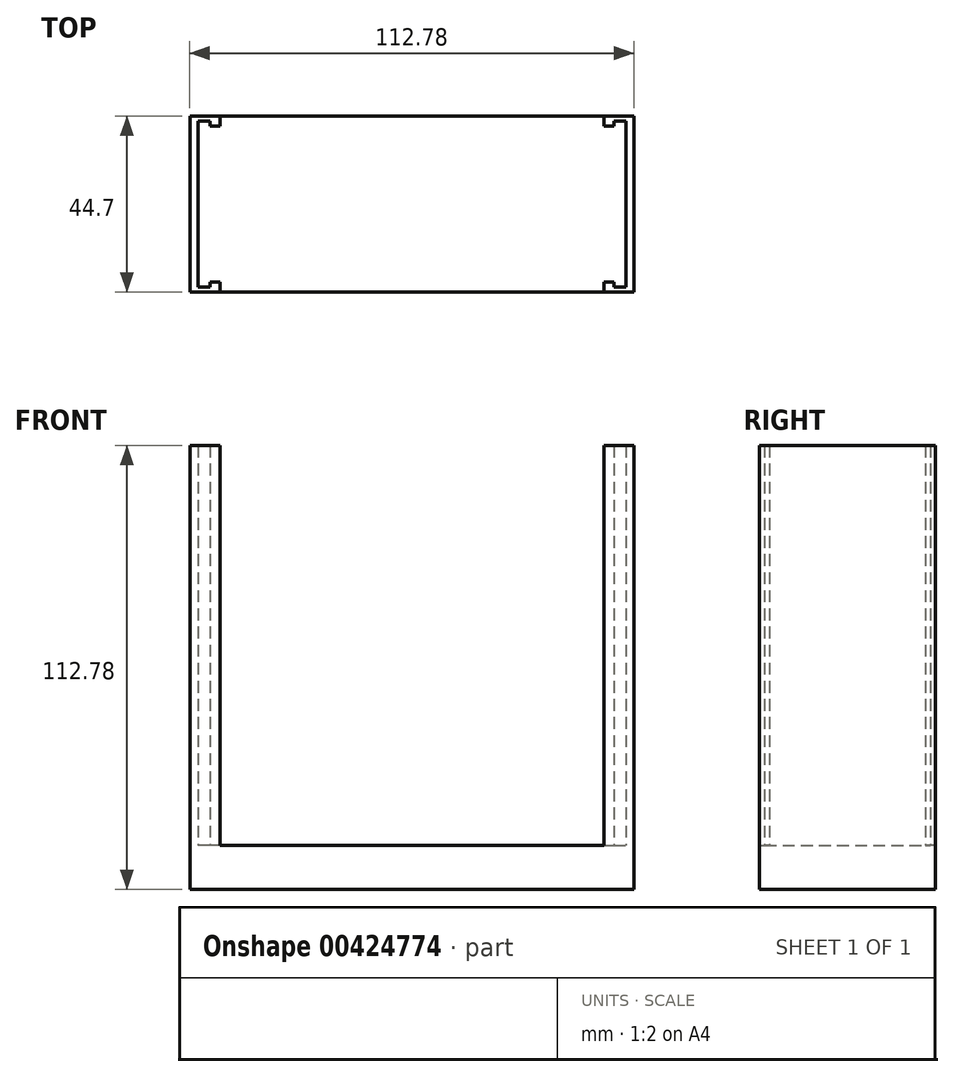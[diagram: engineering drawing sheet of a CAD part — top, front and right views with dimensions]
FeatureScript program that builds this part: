
annotation { "Feature Type Name" : "Feature", "Feature Type Description" : "" }
export const myFeature = defineFeature(function(context is Context, id is Id, definition is map)
    precondition{}
    {
        {
            var Q0;
            Q0=qCreatedBy(makeId("Top.planeOp"),FACE);
            var sketch = newSketch(context, id + "F0", { "sketchPlane" : qUnion([Q0])});
            skLineSegment(sketch, "E0.bottom", {"start": v(-112.78, 0) * mm, "end": v(0, 0) * mm});
            skLineSegment(sketch, "E0.top", {"start": v(-112.78, -44.7) * mm, "end": v(0, -44.7) * mm});
            skLineSegment(sketch, "E0.left", {"start": v(-112.78, 0) * mm, "end": v(-112.78, -44.7) * mm});
            skLineSegment(sketch, "E0.right", {"start": v(0, 0) * mm, "end": v(0, -44.7) * mm});
            skSolve(sketch);
        }
        {
            var Q0;
            Q0 = qSketchRegion(id + "F0", true);
            extrude(context, id + "F1", {"entities" : qUnion([Q0]), "depth" : 11.18 * mm});
        }
        {
            var Q0;
            Q0=makeQuery(id+"F1.opExtrude","CAP_FACE",FACE,{"disambiguationData":[OSD([sQuery(id+"F0.wireOp",EDGE,"E0.bottom"),sQuery(id+"F0.wireOp",EDGE,"E0.top"),sQuery(id+"F0.wireOp",EDGE,"E0.left"),sQuery(id+"F0.wireOp",EDGE,"E0.right")])],"isStart":false});
            var sketch = newSketch(context, id + "F2", { "sketchPlane" : qUnion([Q0])});
            skLineSegment(sketch, "E1", {"start": v(0, -22.35) * mm, "end": v(0, -44.7) * mm});
            skLineSegment(sketch, "E2", {"start": v(0, -44.7) * mm, "end": v(-7.62, -44.7) * mm});
            skLineSegment(sketch, "E3", {"start": v(-7.62, -44.7) * mm, "end": v(-7.62, -42.16) * mm});
            skLineSegment(sketch, "E4", {"start": v(-7.62, -42.16) * mm, "end": v(-5.08, -42.16) * mm});
            skLineSegment(sketch, "E5", {"start": v(-5.08, -42.16) * mm, "end": v(-5.08, -43.43) * mm});
            skLineSegment(sketch, "E6", {"start": v(-5.08, -43.43) * mm, "end": v(-2.03, -43.43) * mm});
            skLineSegment(sketch, "E7", {"start": v(-2.03, -43.43) * mm, "end": v(-2.03, -22.35) * mm});
            skLineSegment(sketch, "E8", {"start": v(0, -22.35) * mm, "end": v(-112.78, -22.35) * mm, "construction": true});
            skLineSegment(sketch, "E9", {"start": v(-56.39, 0) * mm, "end": v(-56.39, -44.7) * mm, "construction": true});
            skLineSegment(sketch, "E10.MirrorCS", {"start": v(-2.03, -1.27) * mm, "end": v(-2.03, -22.35) * mm});
            skLineSegment(sketch, "E11.MirrorCS", {"start": v(0, -22.35) * mm, "end": v(0, 0) * mm});
            skLineSegment(sketch, "E12.MirrorCS", {"start": v(-5.08, -1.27) * mm, "end": v(-2.03, -1.27) * mm});
            skLineSegment(sketch, "E13.MirrorCS", {"start": v(0, 0) * mm, "end": v(-7.62, 0) * mm});
            skLineSegment(sketch, "E14.MirrorCS", {"start": v(-7.62, 0) * mm, "end": v(-7.62, -2.54) * mm});
            skLineSegment(sketch, "E15.MirrorCS", {"start": v(-7.62, -2.54) * mm, "end": v(-5.08, -2.54) * mm});
            skLineSegment(sketch, "E16.MirrorCS", {"start": v(-5.08, -2.54) * mm, "end": v(-5.08, -1.27) * mm});
            skLineSegment(sketch, "E17.MirrorCS", {"start": v(-105.16, 0) * mm, "end": v(-105.16, -2.54) * mm});
            skLineSegment(sketch, "E18.MirrorCS", {"start": v(-105.16, -2.54) * mm, "end": v(-107.7, -2.54) * mm});
            skLineSegment(sketch, "E19.MirrorCS", {"start": v(-107.7, -2.54) * mm, "end": v(-107.7, -1.27) * mm});
            skLineSegment(sketch, "E20.MirrorCS", {"start": v(-107.7, -1.27) * mm, "end": v(-110.74, -1.27) * mm});
            skLineSegment(sketch, "E21.MirrorCS", {"start": v(-112.78, 0) * mm, "end": v(-105.16, 0) * mm});
            skLineSegment(sketch, "E22.MirrorCS", {"start": v(-110.74, -1.27) * mm, "end": v(-110.74, -22.35) * mm});
            skLineSegment(sketch, "E23.MirrorCS", {"start": v(-112.78, -22.35) * mm, "end": v(-112.78, 0) * mm});
            skLineSegment(sketch, "E24.MirrorCS", {"start": v(-112.78, -22.35) * mm, "end": v(-112.78, -44.7) * mm});
            skLineSegment(sketch, "E25.MirrorCS", {"start": v(-110.74, -43.43) * mm, "end": v(-110.74, -22.35) * mm});
            skLineSegment(sketch, "E26.MirrorCS", {"start": v(-107.7, -43.43) * mm, "end": v(-110.74, -43.43) * mm});
            skLineSegment(sketch, "E27.MirrorCS", {"start": v(-112.78, -44.7) * mm, "end": v(-105.16, -44.7) * mm});
            skLineSegment(sketch, "E28.MirrorCS", {"start": v(-105.16, -44.7) * mm, "end": v(-105.16, -42.16) * mm});
            skLineSegment(sketch, "E29.MirrorCS", {"start": v(-105.16, -42.16) * mm, "end": v(-107.7, -42.16) * mm});
            skLineSegment(sketch, "E30.MirrorCS", {"start": v(-107.7, -42.16) * mm, "end": v(-107.7, -43.43) * mm});
            skSolve(sketch);
        }
        {
            var Q0;
            Q0 = qSketchRegion(id + "F2", true);
            extrude(context, id + "F3", {"entities" : qUnion([Q0]), "operationType" : NewBodyOperationType.ADD, "depth" : 101.6 * mm});
        }
    });
